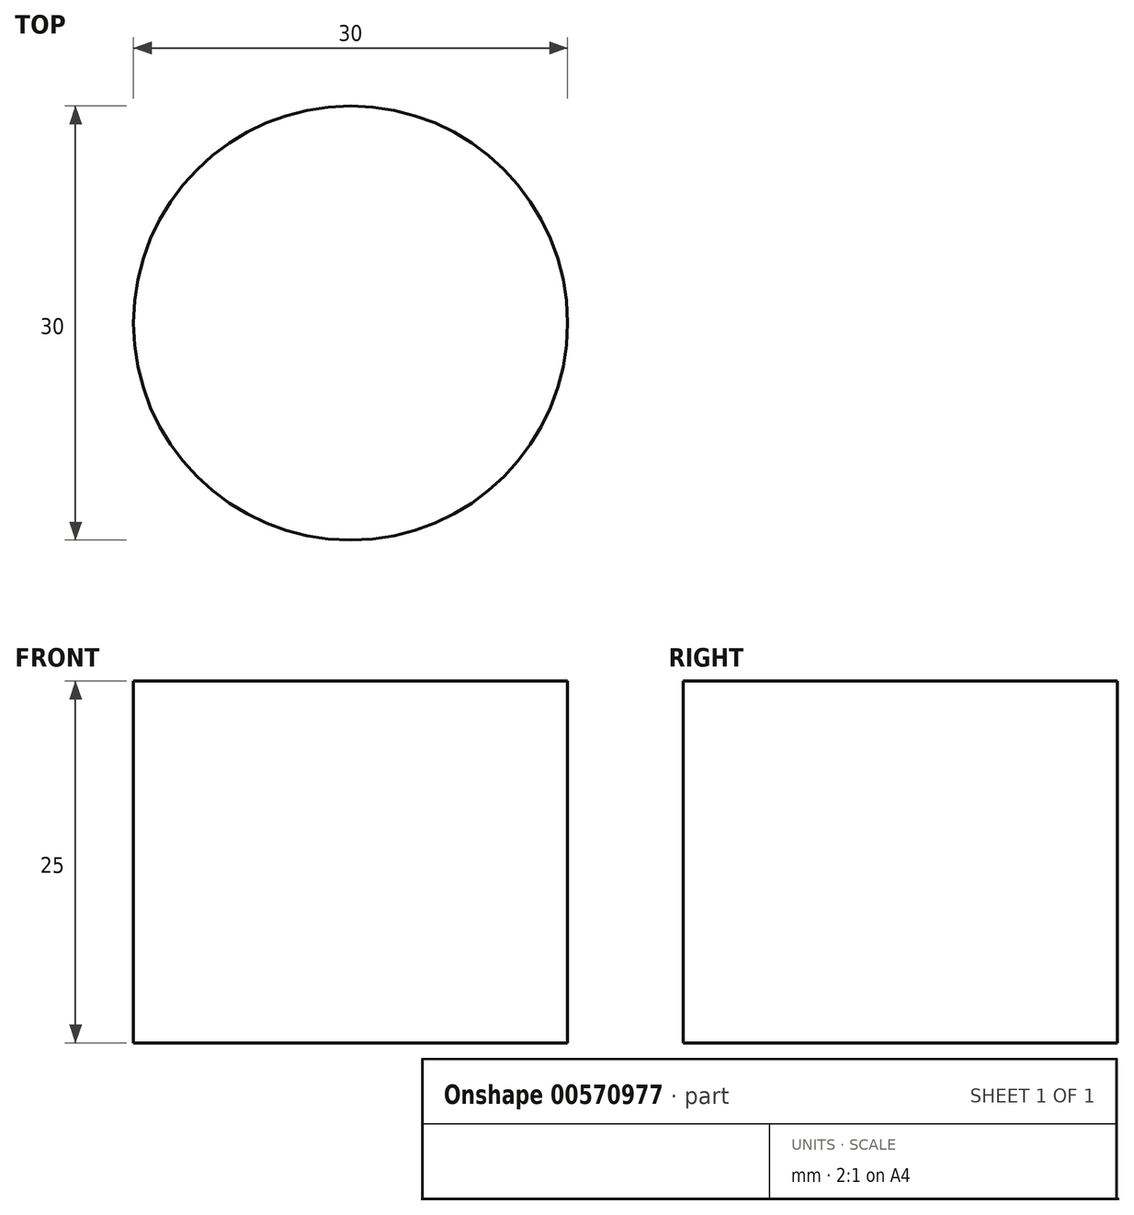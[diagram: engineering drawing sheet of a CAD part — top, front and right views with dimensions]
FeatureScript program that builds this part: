
annotation { "Feature Type Name" : "Feature", "Feature Type Description" : "" }
export const myFeature = defineFeature(function(context is Context, id is Id, definition is map)
    precondition{}
    {
        {
            var Q0;
            Q0=qCreatedBy(makeId("Top.planeOp"),FACE);
            var sketch = newSketch(context, id + "F0", { "sketchPlane" : qUnion([Q0])});
            skCircle(sketch, "E0", {"center": v(-35, -34.75) * mm, "radius": 15 * mm});
            skSolve(sketch);
        }
        {
            var Q0;
            Q0=makeQuery(id+"F0.imprint","IMPRINT",FACE,{"disambiguationData":[TD([[makeQuery(id+"F0.imprint","IMPRINT",EDGE,{"derivedFrom":sQuery(id+"F0.wireOp",EDGE,"E0")}),1.0]])]});
            extrude(context, id + "F1", {"entities" : qUnion([Q0]), "depth" : 25 * mm, "offsetDistance" : 25 * mm});
        }
    });
